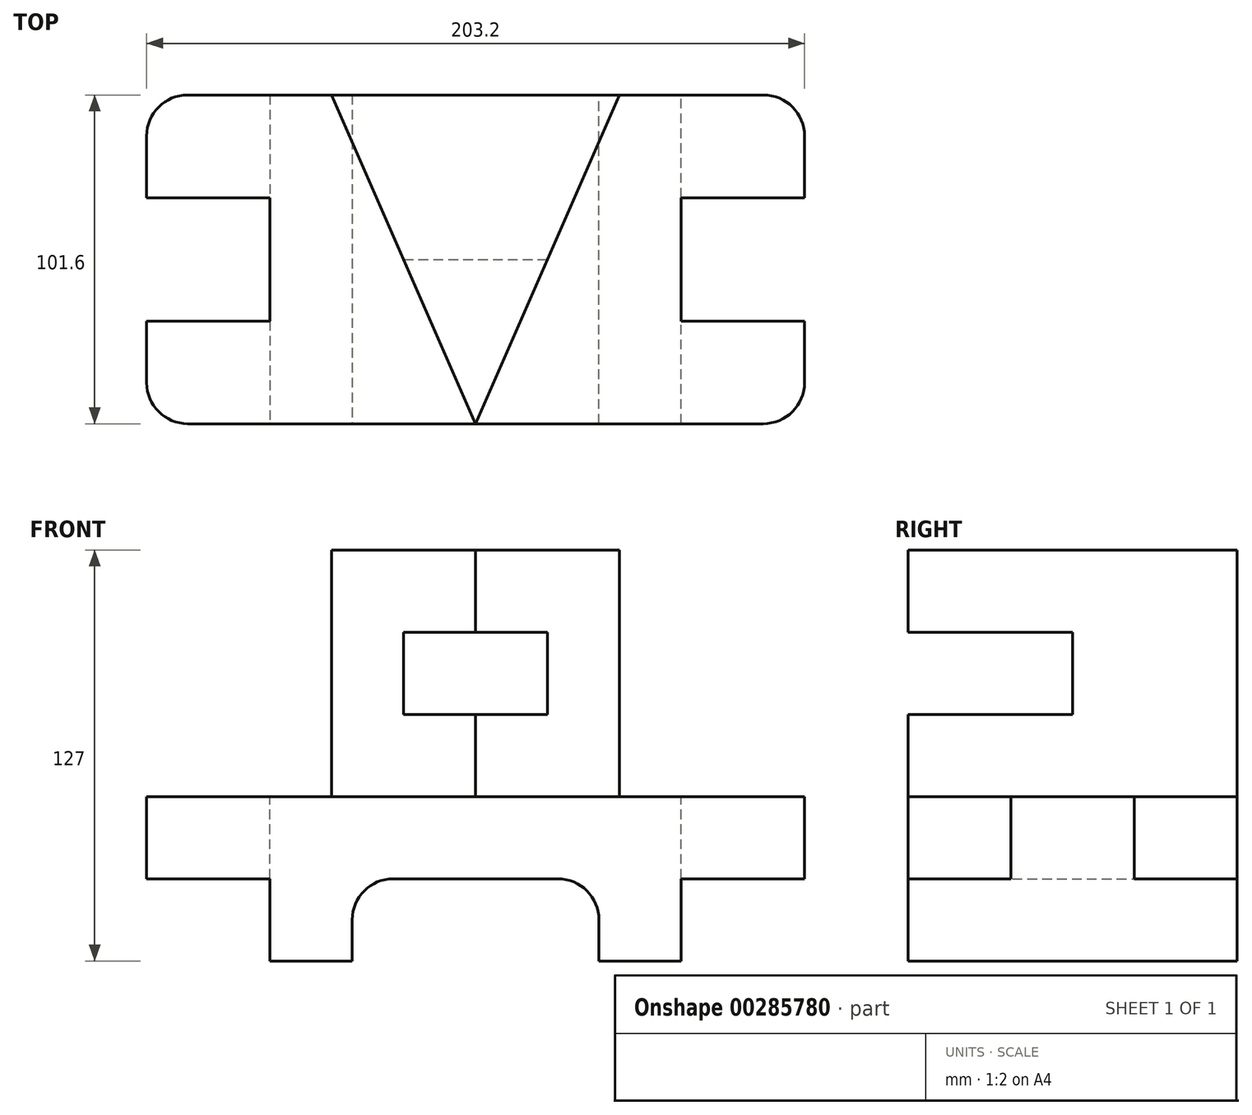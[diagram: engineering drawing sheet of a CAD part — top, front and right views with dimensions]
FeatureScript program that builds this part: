
annotation { "Feature Type Name" : "Feature", "Feature Type Description" : "" }
export const myFeature = defineFeature(function(context is Context, id is Id, definition is map)
    precondition{}
    {
        {
            var Q0;
            Q0=qCreatedBy(makeId("Top.planeOp"),FACE);
            var sketch = newSketch(context, id + "F0", { "sketchPlane" : qUnion([Q0])});
            skLineSegment(sketch, "E0.bottom", {"start": v(-88.9, 0) * mm, "end": v(88.9, 0) * mm});
            skLineSegment(sketch, "E0.top", {"start": v(-88.9, 101.6) * mm, "end": v(88.9, 101.6) * mm});
            skLineSegment(sketch, "E0.left", {"start": v(-101.6, 12.7) * mm, "end": v(-101.6, 88.9) * mm});
            skLineSegment(sketch, "E0.right", {"start": v(101.6, 12.7) * mm, "end": v(101.6, 88.9) * mm});
            skPoint(sketch, "E1.visualSharp", {"position": v(101.6, 101.6) * mm});
            skArc(sketch, "E1.filletArc", {"start": v(101.6, 88.9) * mm, "mid": v(97.88, 97.88) * mm, "end": v(88.9, 101.6) * mm});
            skPoint(sketch, "E2.visualSharp", {"position": v(101.6, 0) * mm});
            skArc(sketch, "E2.filletArc", {"start": v(88.9, 0) * mm, "mid": v(97.88, 3.72) * mm, "end": v(101.6, 12.7) * mm});
            skPoint(sketch, "E3.visualSharp", {"position": v(-101.6, 0) * mm});
            skArc(sketch, "E3.filletArc", {"start": v(-101.6, 12.7) * mm, "mid": v(-97.88, 3.72) * mm, "end": v(-88.9, 0) * mm});
            skPoint(sketch, "E4.visualSharp", {"position": v(-101.6, 101.6) * mm});
            skArc(sketch, "E4.filletArc", {"start": v(-88.9, 101.6) * mm, "mid": v(-97.88, 97.88) * mm, "end": v(-101.6, 88.9) * mm});
            skLineSegment(sketch, "E5.bottom", {"start": v(-101.6, 69.85) * mm, "end": v(-63.5, 69.85) * mm});
            skLineSegment(sketch, "E5.top", {"start": v(-101.6, 31.75) * mm, "end": v(-63.5, 31.75) * mm});
            skLineSegment(sketch, "E5.left", {"start": v(-101.6, 69.85) * mm, "end": v(-101.6, 31.75) * mm});
            skLineSegment(sketch, "E5.right", {"start": v(-63.5, 69.85) * mm, "end": v(-63.5, 31.75) * mm});
            skLineSegment(sketch, "E6.bottom", {"start": v(101.6, 69.85) * mm, "end": v(63.5, 69.85) * mm});
            skLineSegment(sketch, "E6.top", {"start": v(101.6, 31.75) * mm, "end": v(63.5, 31.75) * mm});
            skLineSegment(sketch, "E6.left", {"start": v(101.6, 69.85) * mm, "end": v(101.6, 31.75) * mm});
            skLineSegment(sketch, "E6.right", {"start": v(63.5, 69.85) * mm, "end": v(63.5, 31.75) * mm});
            skLineSegment(sketch, "E7", {"start": v(0, 0) * mm, "end": v(44.45, 101.6) * mm});
            skLineSegment(sketch, "E8", {"start": v(44.45, 101.6) * mm, "end": v(-44.45, 101.6) * mm});
            skLineSegment(sketch, "E9", {"start": v(-44.45, 101.6) * mm, "end": v(0, 0) * mm});
            skSolve(sketch);
        }
        {
            var Q0;
            Q0=makeQuery(id+"F0.imprint","IMPRINT",FACE,{"disambiguationData":[TD([[makeQuery(id+"F0.imprint","IMPRINT",EDGE,{"derivedFrom":sQuery(id+"F0.wireOp",EDGE,"E5.bottom")}),-1.0]])]});
            var Q1;
            Q1=makeQuery(id+"F0.imprint","IMPRINT",FACE,{"disambiguationData":[TD([[makeQuery(id+"F0.imprint","IMPRINT",EDGE,{"derivedFrom":sQuery(id+"F0.wireOp",EDGE,"E6.bottom")}),1.0]])]});
            var Q2;
            Q2=makeQuery(id+"F0.imprint","IMPRINT",FACE,{"disambiguationData":[TD([[makeQuery(id+"F0.imprint","IMPRINT",EDGE,{"derivedFrom":sQuery(id+"F0.wireOp",EDGE,"E0.bottom")}),1.0]])]});
            var Q3;
            Q3=makeQuery(id+"F0.imprint","IMPRINT",FACE,{"disambiguationData":[TD([[makeQuery(id+"F0.imprint","IMPRINT",EDGE,{"derivedFrom":sQuery(id+"F0.wireOp",EDGE,"E7")}),1.0]])]});
            extrude(context, id + "F1", {"entities" : qUnion([Q0, Q1, Q2, Q3]), "oppositeDirection" : true, "depth" : 25.4 * mm});
        }
        {
            var Q0;
            Q0=makeQuery(id+"F0.imprint","IMPRINT",FACE,{"disambiguationData":[TD([[makeQuery(id+"F0.imprint","IMPRINT",EDGE,{"derivedFrom":sQuery(id+"F0.wireOp",EDGE,"E6.bottom")}),1.0]])]});
            var Q1;
            Q1=makeQuery(id+"F0.imprint","IMPRINT",FACE,{"disambiguationData":[TD([[makeQuery(id+"F0.imprint","IMPRINT",EDGE,{"derivedFrom":sQuery(id+"F0.wireOp",EDGE,"E5.bottom")}),-1.0]])]});
            extrude(context, id + "F2", {"entities" : qUnion([Q0, Q1]), "operationType" : NewBodyOperationType.REMOVE, "oppositeDirection" : true, "depth" : 25.4 * mm});
        }
        {
            var Q0;
            Q0=makeQuery(id+"F0.imprint","IMPRINT",FACE,{"disambiguationData":[TD([[makeQuery(id+"F0.imprint","IMPRINT",EDGE,{"derivedFrom":sQuery(id+"F0.wireOp",EDGE,"E7")}),1.0]])]});
            extrude(context, id + "F3", {"entities" : qUnion([Q0]), "depth" : 76.2 * mm});
        }
        {
            var Q0;
            Q0=makeQuery(id+"F1.opExtrude","CAP_FACE",FACE,{"disambiguationData":[OSD([sQuery(id+"F0.wireOp",EDGE,"E0.bottom"),sQuery(id+"F0.wireOp",EDGE,"E0.top"),sQuery(id+"F0.wireOp",EDGE,"E0.left"),sQuery(id+"F0.wireOp",EDGE,"E0.right"),sQuery(id+"F0.wireOp",EDGE,"E1.filletArc"),sQuery(id+"F0.wireOp",EDGE,"E2.filletArc"),sQuery(id+"F0.wireOp",EDGE,"E3.filletArc"),sQuery(id+"F0.wireOp",EDGE,"E4.filletArc"),sQuery(id+"F0.wireOp",EDGE,"E5.left"),sQuery(id+"F0.wireOp",EDGE,"E6.left"),sQuery(id+"F0.wireOp",EDGE,"E8")])],"isStart":false});
            var sketch = newSketch(context, id + "F4", { "sketchPlane" : qUnion([Q0])});
            skLineSegment(sketch, "E10", {"start": v(63.5, -69.85) * mm, "end": v(63.5, -101.6) * mm});
            skLineSegment(sketch, "E11", {"start": v(63.5, -101.6) * mm, "end": v(63.5, 0) * mm});
            skLineSegment(sketch, "E12", {"start": v(63.5, 0) * mm, "end": v(38.1, 0) * mm});
            skLineSegment(sketch, "E13", {"start": v(38.1, 0) * mm, "end": v(38.1, -101.6) * mm});
            skLineSegment(sketch, "E14", {"start": v(38.1, -101.6) * mm, "end": v(63.5, -101.6) * mm});
            skLineSegment(sketch, "E15", {"start": v(-63.5, -31.75) * mm, "end": v(-63.5, 0) * mm});
            skLineSegment(sketch, "E16", {"start": v(-63.5, 0) * mm, "end": v(-63.5, -101.6) * mm});
            skLineSegment(sketch, "E17", {"start": v(-63.5, -101.6) * mm, "end": v(-38.1, -101.6) * mm});
            skLineSegment(sketch, "E18", {"start": v(-38.1, -101.6) * mm, "end": v(-38.1, 0) * mm});
            skLineSegment(sketch, "E19", {"start": v(-38.1, 0) * mm, "end": v(-63.5, 0) * mm});
            skSolve(sketch);
        }
        {
            var Q0;
            {var subQ0=sQuery(id+"F4.wireOp",EDGE,"E17");Q0=makeQuery(id+"F4.imprint","IMPRINT",FACE,{"disambiguationData":[TD([[makeQuery(id+"F4.imprint","IMPRINT",EDGE,{"derivedFrom":subQ0}),1.0]])]});}
            var Q1;
            {var subQ0=sQuery(id+"F4.wireOp",EDGE,"E12");Q1=makeQuery(id+"F4.imprint","IMPRINT",FACE,{"disambiguationData":[TD([[makeQuery(id+"F4.imprint","IMPRINT",EDGE,{"derivedFrom":subQ0}),-1.0]])]});}
            extrude(context, id + "F5", {"entities" : qUnion([Q0, Q1]), "operationType" : NewBodyOperationType.ADD, "depth" : 25.4 * mm});
        }
        {
            var Q0;
            Q0=makeQuery(id+"F5.opExtrude","CAP_EDGE",EDGE,{"disambiguationData":[OSD([sQuery(id+"F4.wireOp",EDGE,"E18")])],"isStart":true});
            var Q1;
            Q1=makeQuery(id+"F5.opExtrude","CAP_EDGE",EDGE,{"disambiguationData":[OSD([sQuery(id+"F4.wireOp",EDGE,"E13")])],"isStart":true});
            fillet(context, id + "F6", {"entities" : qUnion([Q0, Q1]), "radius" : 12.7 * mm, "tangentPropagation" : true, "allowEdgeOverflow" : false});
        }
        {
            var Q0;
            Q0=makeQuery(id+"F5.boolean.opBoolean","MERGE",FACE,{"derivedFrom":[makeQuery(id+"F2.boolean.opBoolean","COPY",FACE,{"derivedFrom":makeQuery(id+"F2.opExtrude","SWEPT_FACE",FACE,{"disambiguationData":[OSD([sQuery(id+"F0.wireOp",EDGE,"E6.right")])]})}),makeQuery(id+"F5.opExtrude","SWEPT_FACE",FACE,{"disambiguationData":[OSD([sQuery(id+"F4.wireOp",EDGE,"E11")])]})]});
            var sketch = newSketch(context, id + "F7", { "sketchPlane" : qUnion([Q0])});
            skLineSegment(sketch, "E20", {"start": v(0, 0) * mm, "end": v(0, 25.4) * mm});
            skLineSegment(sketch, "E21", {"start": v(0, 25.4) * mm, "end": v(50.8, 25.4) * mm});
            skLineSegment(sketch, "E22", {"start": v(50.8, 25.4) * mm, "end": v(50.8, 50.8) * mm});
            skLineSegment(sketch, "E23", {"start": v(50.8, 50.8) * mm, "end": v(0, 50.8) * mm});
            skLineSegment(sketch, "E24", {"start": v(0, 50.8) * mm, "end": v(0, 25.4) * mm});
            skSolve(sketch);
        }
        {
            var Q0;
            Q0=makeQuery(id+"F7.imprint","IMPRINT",FACE,{"disambiguationData":[TD([[makeQuery(id+"F7.imprint","IMPRINT",EDGE,{"derivedFrom":sQuery(id+"F7.wireOp",EDGE,"E21")}),1.0]])]});
            extrude(context, id + "F8", {"entities" : qUnion([Q0]), "operationType" : NewBodyOperationType.REMOVE, "endBound" : BoundingType.THROUGH_ALL, "oppositeDirection" : true, "depth" : 25.4 * mm});
        }
    });
